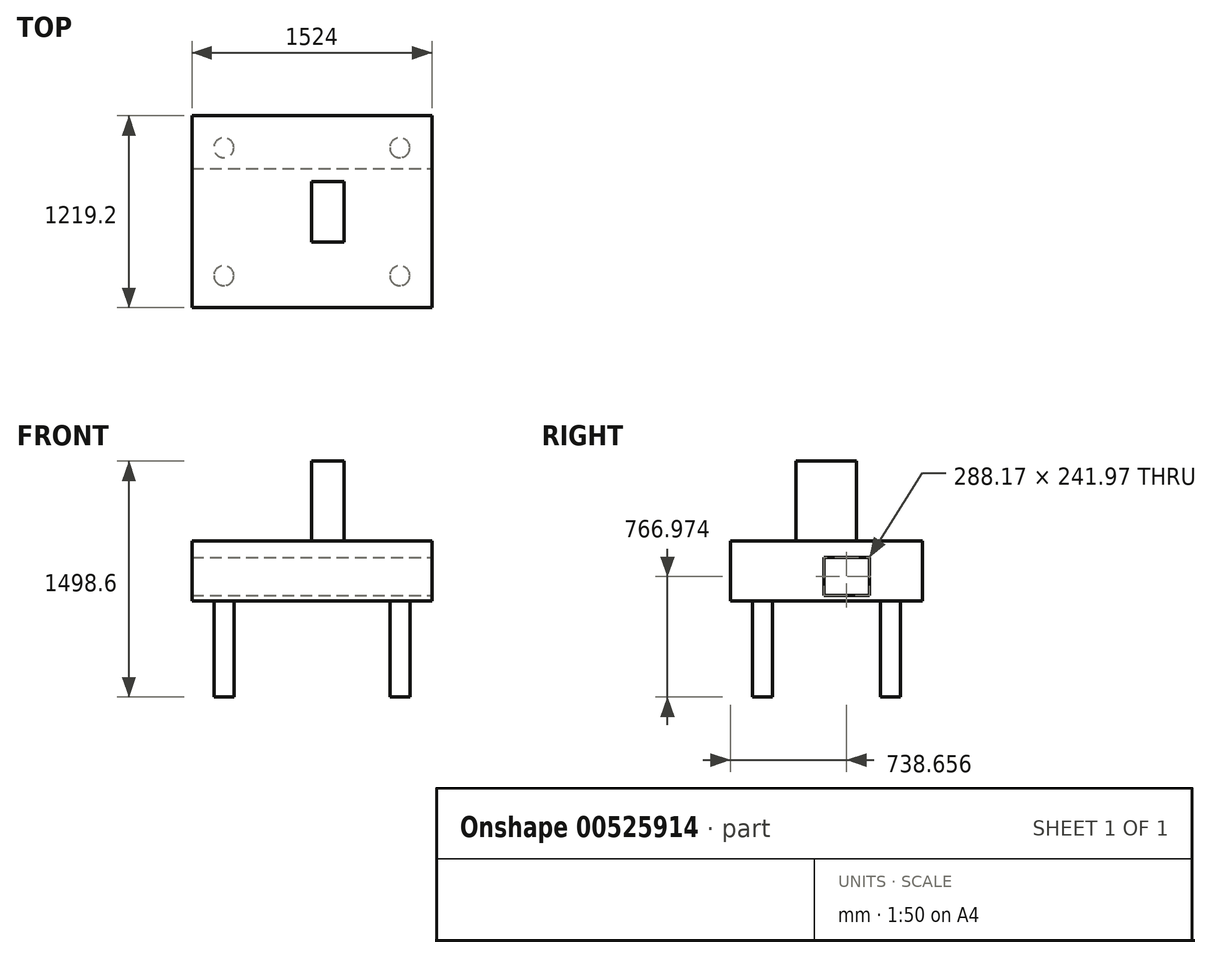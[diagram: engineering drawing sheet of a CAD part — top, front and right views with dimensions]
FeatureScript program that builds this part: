
annotation { "Feature Type Name" : "Feature", "Feature Type Description" : "" }
export const myFeature = defineFeature(function(context is Context, id is Id, definition is map)
    precondition{}
    {
        {
            var Q0;
            Q0=qCreatedBy(makeId("Top.planeOp"),FACE);
            var sketch = newSketch(context, id + "F0", { "sketchPlane" : qUnion([Q0])});
            skLineSegment(sketch, "E0.bottom", {"start": v(762, 609.6) * mm, "end": v(-762, 609.6) * mm});
            skLineSegment(sketch, "E0.top", {"start": v(762, -609.6) * mm, "end": v(-762, -609.6) * mm});
            skLineSegment(sketch, "E0.left", {"start": v(762, 609.6) * mm, "end": v(762, -609.6) * mm});
            skLineSegment(sketch, "E0.right", {"start": v(-762, 609.6) * mm, "end": v(-762, -609.6) * mm});
            skPoint(sketch, "E0.middle", {"position": v(0, 0) * mm});
            skSolve(sketch);
        }
        {
            var Q0;
            Q0 = qSketchRegion(id + "F0", true);
            extrude(context, id + "F1", {"entities" : qUnion([Q0]), "depth" : 381 * mm, "offsetDistance" : 25.4 * mm});
        }
        {
            var Q0;
            Q0=makeQuery(id+"F1.opExtrude","CAP_FACE",FACE,{"disambiguationData":[OSD([sQuery(id+"F0.wireOp",EDGE,"E0.bottom"),sQuery(id+"F0.wireOp",EDGE,"E0.top"),sQuery(id+"F0.wireOp",EDGE,"E0.left"),sQuery(id+"F0.wireOp",EDGE,"E0.right")])],"isStart":true});
            var sketch = newSketch(context, id + "F2", { "sketchPlane" : qUnion([Q0])});
            skCircle(sketch, "E1", {"center": v(-558.8, -406.4) * mm, "radius": 63.5 * mm});
            skCircle(sketch, "E2", {"center": v(-558.8, 406.4) * mm, "radius": 63.5 * mm});
            skCircle(sketch, "E3", {"center": v(558.8, -406.4) * mm, "radius": 63.5 * mm});
            skCircle(sketch, "E4", {"center": v(558.8, 406.4) * mm, "radius": 63.5 * mm});
            skLineSegment(sketch, "E5", {"start": v(-558.8, -406.4) * mm, "end": v(-558.8, 406.4) * mm, "construction": true});
            skLineSegment(sketch, "E6", {"start": v(-558.8, 406.4) * mm, "end": v(558.8, 406.4) * mm, "construction": true});
            skLineSegment(sketch, "E7", {"start": v(558.8, 406.4) * mm, "end": v(558.8, -406.4) * mm, "construction": true});
            skLineSegment(sketch, "E8", {"start": v(558.8, -406.4) * mm, "end": v(-558.8, -406.4) * mm, "construction": true});
            skSolve(sketch);
        }
        {
            var Q0;
            Q0=makeQuery(id+"F2.imprint","IMPRINT",FACE,{"disambiguationData":[TD([[makeQuery(id+"F2.imprint","IMPRINT",EDGE,{"derivedFrom":sQuery(id+"F2.wireOp",EDGE,"E1")}),1.0]])]});
            var Q1;
            Q1=makeQuery(id+"F2.imprint","IMPRINT",FACE,{"disambiguationData":[TD([[makeQuery(id+"F2.imprint","IMPRINT",EDGE,{"derivedFrom":sQuery(id+"F2.wireOp",EDGE,"E2")}),1.0]])]});
            var Q2;
            Q2=makeQuery(id+"F2.imprint","IMPRINT",FACE,{"disambiguationData":[TD([[makeQuery(id+"F2.imprint","IMPRINT",EDGE,{"derivedFrom":sQuery(id+"F2.wireOp",EDGE,"E4")}),1.0]])]});
            var Q3;
            Q3=makeQuery(id+"F2.imprint","IMPRINT",FACE,{"disambiguationData":[TD([[makeQuery(id+"F2.imprint","IMPRINT",EDGE,{"derivedFrom":sQuery(id+"F2.wireOp",EDGE,"E3")}),1.0]])]});
            extrude(context, id + "F3", {"entities" : qUnion([Q0, Q1, Q2, Q3]), "operationType" : NewBodyOperationType.ADD, "depth" : 609.6 * mm, "offsetDistance" : 25.4 * mm});
        }
        {
            var Q0;
            Q0=makeQuery(id+"F1.opExtrude","SWEPT_FACE",FACE,{"disambiguationData":[OSD([sQuery(id+"F0.wireOp",EDGE,"E0.left")])]});
            var sketch = newSketch(context, id + "F4", { "sketchPlane" : qUnion([Q0])});
            skLineSegment(sketch, "E9.bottom", {"start": v(273.14, 36.4) * mm, "end": v(-15.03, 36.4) * mm});
            skLineSegment(sketch, "E9.top", {"start": v(273.14, 278.36) * mm, "end": v(-15.03, 278.36) * mm});
            skLineSegment(sketch, "E9.left", {"start": v(273.14, 36.4) * mm, "end": v(273.14, 278.36) * mm});
            skLineSegment(sketch, "E9.right", {"start": v(-15.03, 36.4) * mm, "end": v(-15.03, 278.36) * mm});
            skPoint(sketch, "E9.middle", {"position": v(129.06, 157.37) * mm});
            skSolve(sketch);
        }
        {
            var Q0;
            Q0 = qSketchRegion(id + "F4", true);
            extrude(context, id + "F5", {"entities" : qUnion([Q0]), "operationType" : NewBodyOperationType.REMOVE, "endBound" : BoundingType.UP_TO_NEXT, "oppositeDirection" : true, "depth" : 25.4 * mm, "offsetDistance" : 25.4 * mm});
        }
        {
            assignVariable(context, id + "F6", {"name" : "height", "anyValue" : 508 * mm});
        }
        {
            var Q0;
            Q0=makeQuery(id+"F1.opExtrude","CAP_FACE",FACE,{"disambiguationData":[OSD([sQuery(id+"F0.wireOp",EDGE,"E0.bottom"),sQuery(id+"F0.wireOp",EDGE,"E0.top"),sQuery(id+"F0.wireOp",EDGE,"E0.left"),sQuery(id+"F0.wireOp",EDGE,"E0.right")])],"isStart":false});
            var sketch = newSketch(context, id + "F7", { "sketchPlane" : qUnion([Q0])});
            skLineSegment(sketch, "E10.bottom", {"start": v(0, -192.6) * mm, "end": v(205.61, -192.6) * mm});
            skLineSegment(sketch, "E10.top", {"start": v(0, 192.6) * mm, "end": v(205.61, 192.6) * mm});
            skLineSegment(sketch, "E10.left", {"start": v(0, -192.6) * mm, "end": v(0, 192.6) * mm});
            skLineSegment(sketch, "E10.right", {"start": v(205.61, -192.6) * mm, "end": v(205.61, 192.6) * mm});
            skPoint(sketch, "E10.middle", {"position": v(102.8, 0) * mm});
            skSolve(sketch);
        }
        {
            var Q0;
            Q0 = qSketchRegion(id + "F7", true);
            extrude(context, id + "F8", {"entities" : qUnion([Q0]), "operationType" : NewBodyOperationType.ADD, "depth" : getVariable(context, 'height'), "offsetDistance" : 25.4 * mm});
        }
    });
